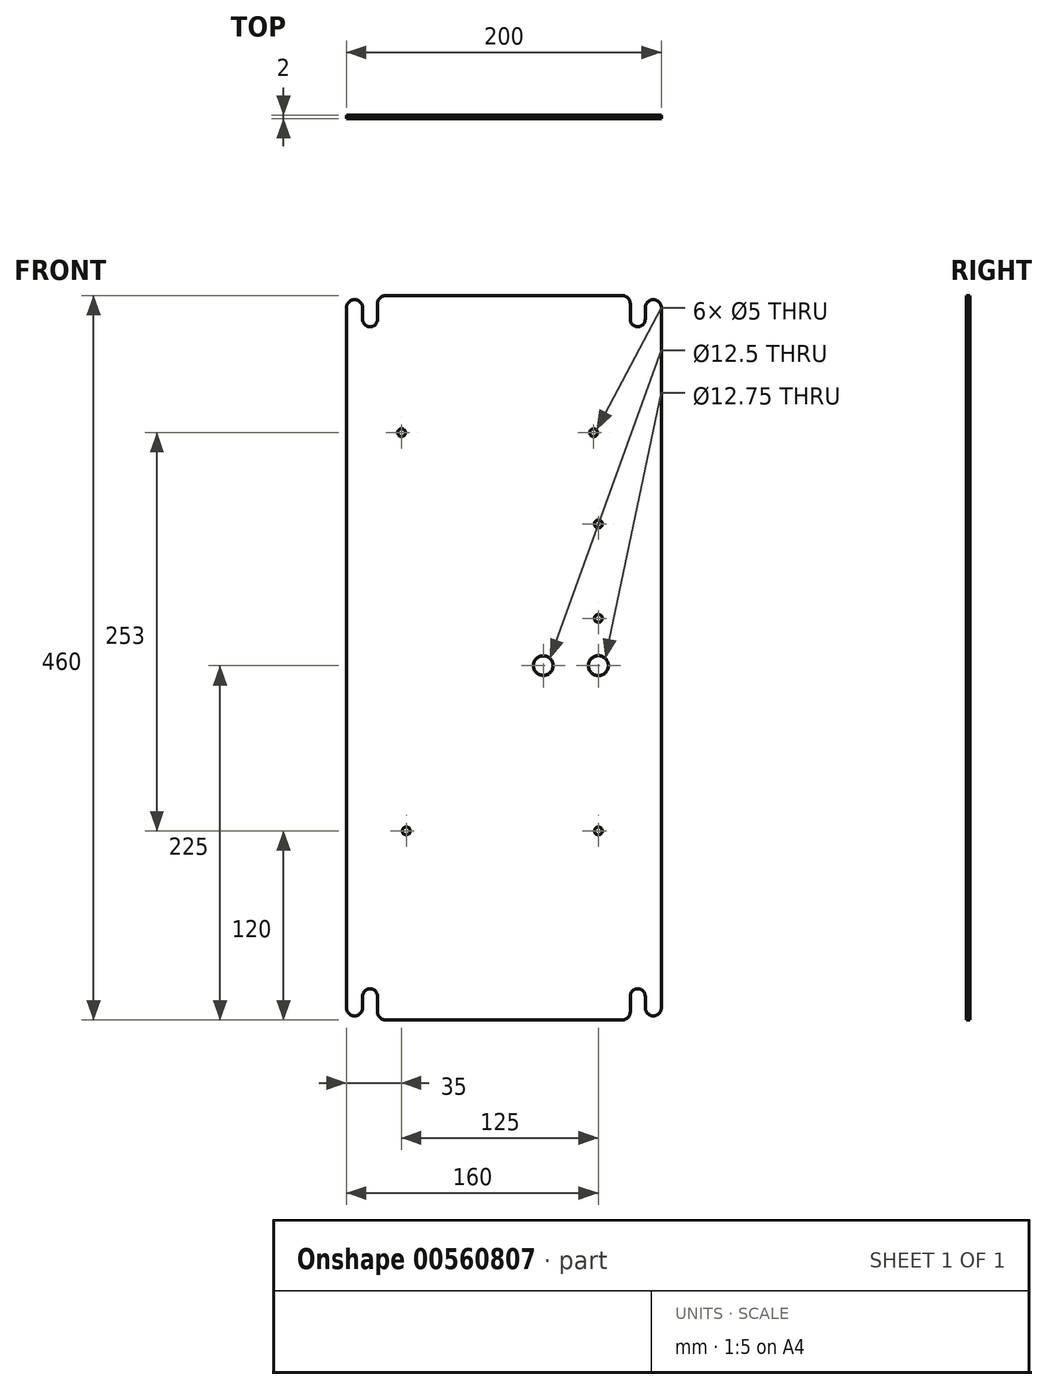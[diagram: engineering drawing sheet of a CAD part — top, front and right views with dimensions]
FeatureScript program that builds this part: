
annotation { "Feature Type Name" : "Feature", "Feature Type Description" : "" }
export const myFeature = defineFeature(function(context is Context, id is Id, definition is map)
    precondition{}
    {
        {
            var Q0;
            Q0=qCreatedBy(makeId("Front.planeOp"),FACE);
            var sketch = newSketch(context, id + "F0", { "sketchPlane" : qUnion([Q0])});
            skLineSegment(sketch, "E0.top", {"start": v(-75.25, -230) * mm, "end": v(75.25, -230) * mm});
            skLineSegment(sketch, "E0.left", {"start": v(-100, 222.5) * mm, "end": v(-100, -222.5) * mm});
            skLineSegment(sketch, "E0.right", {"start": v(100, 222.5) * mm, "end": v(100, -222.5) * mm});
            skPoint(sketch, "E0.middle", {"position": v(0, 0) * mm});
            skArc(sketch, "E1", {"start": v(-89.75, 215) * mm, "mid": v(-85, 210.25) * mm, "end": v(-80.25, 215) * mm});
            skArc(sketch, "E2.MirrorC", {"start": v(89.75, 215) * mm, "mid": v(85, 210.25) * mm, "end": v(80.25, 215) * mm});
            skArc(sketch, "E3.MirrorC", {"start": v(-89.75, -215) * mm, "mid": v(-85, -210.25) * mm, "end": v(-80.25, -215) * mm});
            skArc(sketch, "E4.MirrorC", {"start": v(89.75, -215) * mm, "mid": v(85, -210.25) * mm, "end": v(80.25, -215) * mm});
            skLineSegment(sketch, "E5", {"start": v(-89.75, 215) * mm, "end": v(-89.75, 222.5) * mm});
            skLineSegment(sketch, "E6", {"start": v(-80.25, 215) * mm, "end": v(-80.25, 225) * mm});
            skLineSegment(sketch, "E7.trimOffspring", {"start": v(-75.25, 230) * mm, "end": v(75.25, 230) * mm});
            skArc(sketch, "E8", {"start": v(-89.75, 222.5) * mm, "mid": v(-94.87, 227.5) * mm, "end": v(-100, 222.5) * mm});
            skPoint(sketch, "E8.endSnap0", {"position": v(-89.75, 222.5) * mm});
            skPoint(sketch, "E0.bottom.end.orphan", {"position": v(-89.75, 230) * mm});
            skPoint(sketch, "E9.orphan", {"position": v(-100, 230) * mm});
            skPoint(sketch, "E10.visualSharp", {"position": v(-80.25, 230) * mm});
            skArc(sketch, "E10.filletArc", {"start": v(-75.25, 230) * mm, "mid": v(-78.79, 228.54) * mm, "end": v(-80.25, 225) * mm});
            skLineSegment(sketch, "E11.MirrorCS", {"start": v(80.25, 215) * mm, "end": v(80.25, 225) * mm});
            skArc(sketch, "E12.MirrorCS", {"start": v(75.25, 230) * mm, "mid": v(78.79, 228.54) * mm, "end": v(80.25, 225) * mm});
            skLineSegment(sketch, "E13.MirrorCS", {"start": v(89.75, 215) * mm, "end": v(89.75, 222.5) * mm});
            skArc(sketch, "E14.MirrorCS", {"start": v(89.75, 222.5) * mm, "mid": v(94.87, 227.5) * mm, "end": v(100, 222.5) * mm});
            skLineSegment(sketch, "E15.MirrorCS", {"start": v(75.25, 230) * mm, "end": v(-75.25, 230) * mm});
            skPoint(sketch, "E16.MirrorP", {"position": v(89.75, 222.5) * mm});
            skPoint(sketch, "E17.MirrorP", {"position": v(100, 230) * mm});
            skPoint(sketch, "E18.MirrorP", {"position": v(80.25, 230) * mm});
            skPoint(sketch, "E19.MirrorP", {"position": v(89.75, 230) * mm});
            skLineSegment(sketch, "E20.MirrorCS", {"start": v(89.75, -215) * mm, "end": v(89.75, -222.5) * mm});
            skPoint(sketch, "E21.MirrorP", {"position": v(100, -230) * mm});
            skArc(sketch, "E22.MirrorCS", {"start": v(75.25, -230) * mm, "mid": v(78.79, -228.54) * mm, "end": v(80.25, -225) * mm});
            skLineSegment(sketch, "E23.MirrorCS", {"start": v(100, -222.5) * mm, "end": v(100, 222.5) * mm});
            skPoint(sketch, "E24.MirrorP", {"position": v(89.75, -230) * mm});
            skPoint(sketch, "E25.MirrorP", {"position": v(80.25, -230) * mm});
            skLineSegment(sketch, "E26.MirrorCS", {"start": v(75.25, -230) * mm, "end": v(-75.25, -230) * mm});
            skLineSegment(sketch, "E27.MirrorCS", {"start": v(80.25, -215) * mm, "end": v(80.25, -225) * mm});
            skPoint(sketch, "E28.MirrorP", {"position": v(89.75, -222.5) * mm});
            skArc(sketch, "E29.MirrorCS", {"start": v(89.75, -222.5) * mm, "mid": v(94.87, -227.5) * mm, "end": v(100, -222.5) * mm});
            skLineSegment(sketch, "E30.MirrorCS", {"start": v(-89.75, -215) * mm, "end": v(-89.75, -222.5) * mm});
            skLineSegment(sketch, "E31.MirrorCS", {"start": v(-80.25, -215) * mm, "end": v(-80.25, -225) * mm});
            skArc(sketch, "E32.MirrorCS", {"start": v(-89.75, -222.5) * mm, "mid": v(-94.87, -227.5) * mm, "end": v(-100, -222.5) * mm});
            skArc(sketch, "E33.MirrorCS", {"start": v(-75.25, -230) * mm, "mid": v(-78.79, -228.54) * mm, "end": v(-80.25, -225) * mm});
            skLineSegment(sketch, "E34.MirrorCS", {"start": v(75.25, -230) * mm, "end": v(-100, -230) * mm});
            skPoint(sketch, "E35.MirrorP", {"position": v(-80.25, -230) * mm});
            skPoint(sketch, "E36.MirrorP", {"position": v(-89.75, -222.5) * mm});
            skPoint(sketch, "E37.MirrorP", {"position": v(-89.75, -230) * mm});
            skLineSegment(sketch, "E38.MirrorCS", {"start": v(-100, -222.5) * mm, "end": v(-100, 222.5) * mm});
            skPoint(sketch, "E39.MirrorP", {"position": v(-100, -230) * mm});
            skSolve(sketch);
        }
        {
            var Q0;
            Q0 = qSketchRegion(id + "F0", true);
            extrude(context, id + "F1", {"entities" : qUnion([Q0]), "depth" : 2 * mm, "offsetDistance" : 25 * mm});
        }
        {
            var Q0;
            Q0=makeQuery(id+"F1.opExtrude","CAP_FACE",FACE,{"disambiguationData":[OSD([sQuery(id+"F0.wireOp",EDGE,"E1"),sQuery(id+"F0.wireOp",EDGE,"E5"),sQuery(id+"F0.wireOp",EDGE,"E6"),sQuery(id+"F0.wireOp",EDGE,"E8"),sQuery(id+"F0.wireOp",EDGE,"E10.filletArc"),sQuery(id+"F0.wireOp",EDGE,"E11.MirrorCS"),sQuery(id+"F0.wireOp",EDGE,"E12.MirrorCS"),sQuery(id+"F0.wireOp",EDGE,"E13.MirrorCS"),sQuery(id+"F0.wireOp",EDGE,"E14.MirrorCS"),sQuery(id+"F0.wireOp",EDGE,"E15.MirrorCS"),sQuery(id+"F0.wireOp",EDGE,"E2.MirrorC"),sQuery(id+"F0.wireOp",EDGE,"E20.MirrorCS"),sQuery(id+"F0.wireOp",EDGE,"E22.MirrorCS"),sQuery(id+"F0.wireOp",EDGE,"E4.MirrorC"),sQuery(id+"F0.wireOp",EDGE,"E27.MirrorCS"),sQuery(id+"F0.wireOp",EDGE,"E23.MirrorCS"),sQuery(id+"F0.wireOp",EDGE,"E29.MirrorCS"),sQuery(id+"F0.wireOp",EDGE,"E3.MirrorC"),sQuery(id+"F0.wireOp",EDGE,"E30.MirrorCS"),sQuery(id+"F0.wireOp",EDGE,"E31.MirrorCS"),sQuery(id+"F0.wireOp",EDGE,"E32.MirrorCS"),sQuery(id+"F0.wireOp",EDGE,"E33.MirrorCS"),sQuery(id+"F0.wireOp",EDGE,"E34.MirrorCS"),sQuery(id+"F0.wireOp",EDGE,"E38.MirrorCS")])],"isStart":false});
            var sketch = newSketch(context, id + "F2", { "sketchPlane" : qUnion([Q0])});
            skCircle(sketch, "E40", {"center": v(25, -5) * mm, "radius": 6.25 * mm});
            skSolve(sketch);
        }
        {
            var Q0;
            Q0 = qSketchRegion(id + "F2", true);
            extrude(context, id + "F3", {"entities" : qUnion([Q0]), "operationType" : NewBodyOperationType.REMOVE, "endBound" : BoundingType.THROUGH_ALL, "oppositeDirection" : true, "depth" : 25 * mm, "offsetDistance" : 25 * mm});
        }
        {
            var Q0;
            Q0=makeQuery(id+"F1.opExtrude","CAP_FACE",FACE,{"disambiguationData":[OSD([sQuery(id+"F0.wireOp",EDGE,"E1"),sQuery(id+"F0.wireOp",EDGE,"E5"),sQuery(id+"F0.wireOp",EDGE,"E6"),sQuery(id+"F0.wireOp",EDGE,"E8"),sQuery(id+"F0.wireOp",EDGE,"E10.filletArc"),sQuery(id+"F0.wireOp",EDGE,"E11.MirrorCS"),sQuery(id+"F0.wireOp",EDGE,"E12.MirrorCS"),sQuery(id+"F0.wireOp",EDGE,"E13.MirrorCS"),sQuery(id+"F0.wireOp",EDGE,"E14.MirrorCS"),sQuery(id+"F0.wireOp",EDGE,"E15.MirrorCS"),sQuery(id+"F0.wireOp",EDGE,"E2.MirrorC"),sQuery(id+"F0.wireOp",EDGE,"E20.MirrorCS"),sQuery(id+"F0.wireOp",EDGE,"E22.MirrorCS"),sQuery(id+"F0.wireOp",EDGE,"E4.MirrorC"),sQuery(id+"F0.wireOp",EDGE,"E27.MirrorCS"),sQuery(id+"F0.wireOp",EDGE,"E23.MirrorCS"),sQuery(id+"F0.wireOp",EDGE,"E29.MirrorCS"),sQuery(id+"F0.wireOp",EDGE,"E3.MirrorC"),sQuery(id+"F0.wireOp",EDGE,"E30.MirrorCS"),sQuery(id+"F0.wireOp",EDGE,"E31.MirrorCS"),sQuery(id+"F0.wireOp",EDGE,"E32.MirrorCS"),sQuery(id+"F0.wireOp",EDGE,"E33.MirrorCS"),sQuery(id+"F0.wireOp",EDGE,"E34.MirrorCS"),sQuery(id+"F0.wireOp",EDGE,"E38.MirrorCS")])],"isStart":false});
            var sketch = newSketch(context, id + "F4", { "sketchPlane" : qUnion([Q0])});
            skCircle(sketch, "E41", {"center": v(-62, -110) * mm, "radius": 2.5 * mm});
            skCircle(sketch, "E42", {"center": v(60, -110) * mm, "radius": 2.5 * mm});
            skCircle(sketch, "E43", {"center": v(60, -5) * mm, "radius": 6.38 * mm});
            skCircle(sketch, "E44", {"center": v(60, 25) * mm, "radius": 2.5 * mm});
            skCircle(sketch, "E45", {"center": v(60, 85) * mm, "radius": 2.5 * mm});
            skCircle(sketch, "E46", {"center": v(-65, 143) * mm, "radius": 2.5 * mm});
            skCircle(sketch, "E47", {"center": v(57, 143) * mm, "radius": 2.5 * mm});
            skSolve(sketch);
        }
        {
            var Q0;
            Q0 = qSketchRegion(id + "F4", true);
            extrude(context, id + "F5", {"entities" : qUnion([Q0]), "operationType" : NewBodyOperationType.REMOVE, "oppositeDirection" : true, "depth" : 25 * mm, "offsetDistance" : 25 * mm});
        }
    });
